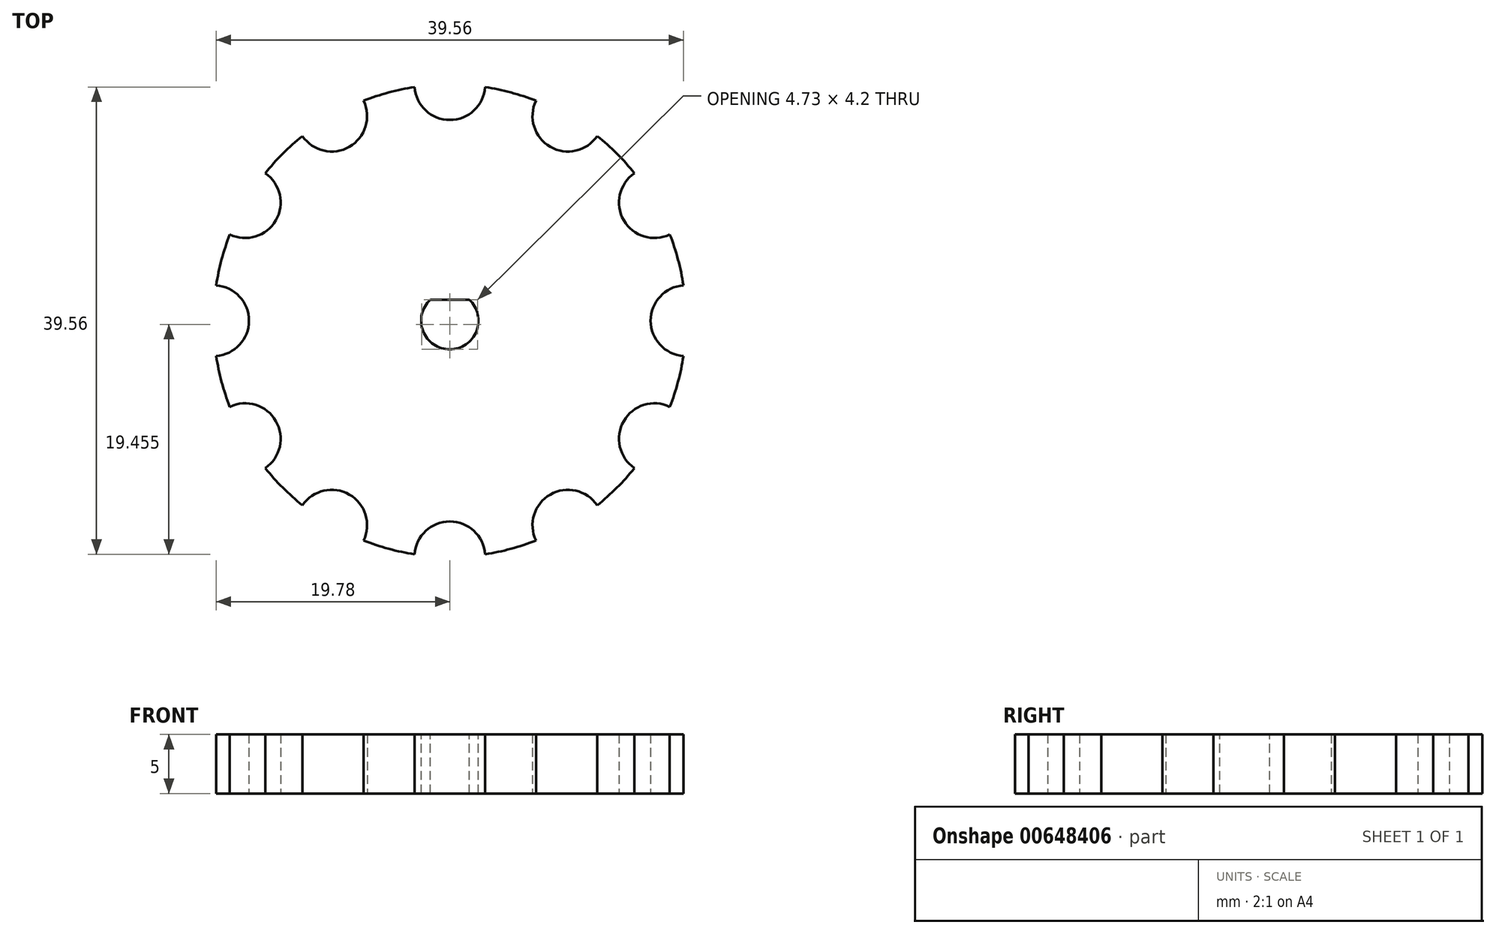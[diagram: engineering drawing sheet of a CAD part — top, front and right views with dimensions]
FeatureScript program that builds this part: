
annotation { "Feature Type Name" : "Feature", "Feature Type Description" : "" }
export const myFeature = defineFeature(function(context is Context, id is Id, definition is map)
    precondition{}
    {
        {
            var Q0;
            Q0=qCreatedBy(makeId("Top.planeOp"),FACE);
            var sketch = newSketch(context, id + "F0", { "sketchPlane" : qUnion([Q0])});
            skCircle(sketch, "E0", {"center": v(0, 0) * mm, "radius": 20 * mm});
            skCircle(sketch, "E1", {"center": v(0, 20) * mm, "radius": 3 * mm});
            skCircle(sketch, "E2.1.0", {"center": v(-10, 17.32) * mm, "radius": 3 * mm});
            skCircle(sketch, "E2.2.0", {"center": v(-17.32, 10) * mm, "radius": 3 * mm});
            skCircle(sketch, "E2.3.0", {"center": v(-20, 0) * mm, "radius": 3 * mm});
            skCircle(sketch, "E2.4.0", {"center": v(-17.32, -10) * mm, "radius": 3 * mm});
            skCircle(sketch, "E2.5.0", {"center": v(-10, -17.32) * mm, "radius": 3 * mm});
            skCircle(sketch, "E2.6.0", {"center": v(0, -20) * mm, "radius": 3 * mm});
            skCircle(sketch, "E2.7.0", {"center": v(10, -17.32) * mm, "radius": 3 * mm});
            skCircle(sketch, "E2.8.0", {"center": v(17.32, -10) * mm, "radius": 3 * mm});
            skCircle(sketch, "E2.9.0", {"center": v(20, 0) * mm, "radius": 3 * mm});
            skCircle(sketch, "E2.10.0", {"center": v(17.32, 10) * mm, "radius": 3 * mm});
            skCircle(sketch, "E2.11.0", {"center": v(10, 17.32) * mm, "radius": 3 * mm});
            skSolve(sketch);
        }
        {
            var Q0;
            {var subQ1=sQuery(id+"F0.wireOp",EDGE,"E0");var subQ33=sQuery(id+"F0.wireOp",EDGE,"E2.10.0");var subQ36=makeQuery(id+"F0.imprint","INTERSECT",VERTEX,{"disambiguationData":[OD(0.0)],"derivedFrom":[subQ1,subQ33]});Q0=makeQuery(id+"F0.imprint","IMPRINT",FACE,{"disambiguationData":[TD([[makeQuery(id+"F0.imprint","IMPRINT",EDGE,{"disambiguationData":[TD([[subQ36,1.0]])],"derivedFrom":subQ1}),1.0]])]});}
            extrude(context, id + "F1", {"entities" : qUnion([Q0]), "depth" : 5 * mm, "offsetDistance" : 25 * mm});
        }
        {
            var Q0;
            Q0=makeQuery(id+"F1.opExtrude","CAP_FACE",FACE,{"disambiguationData":[OSD([sQuery(id+"F0.wireOp",EDGE,"E0"),sQuery(id+"F0.wireOp",EDGE,"E1"),sQuery(id+"F0.wireOp",EDGE,"E2.1.0"),sQuery(id+"F0.wireOp",EDGE,"E2.2.0"),sQuery(id+"F0.wireOp",EDGE,"E2.3.0"),sQuery(id+"F0.wireOp",EDGE,"E2.4.0"),sQuery(id+"F0.wireOp",EDGE,"E2.5.0"),sQuery(id+"F0.wireOp",EDGE,"E2.6.0"),sQuery(id+"F0.wireOp",EDGE,"E2.7.0"),sQuery(id+"F0.wireOp",EDGE,"E2.8.0"),sQuery(id+"F0.wireOp",EDGE,"E2.9.0"),sQuery(id+"F0.wireOp",EDGE,"E2.10.0"),sQuery(id+"F0.wireOp",EDGE,"E2.11.0")])],"isStart":false});
            var sketch = newSketch(context, id + "F2", { "sketchPlane" : qUnion([Q0])});
            skArc(sketch, "E3", {"start": v(-1.65, 1.78) * mm, "mid": v(0, -2.43) * mm, "end": v(1.65, 1.78) * mm});
            skLineSegment(sketch, "E4", {"start": v(-1.65, 1.78) * mm, "end": v(1.65, 1.78) * mm});
            skSolve(sketch);
        }
        {
            var Q0;
            Q0=makeQuery(id+"F2.imprint","IMPRINT",FACE,{"disambiguationData":[TD([[makeQuery(id+"F2.imprint","IMPRINT",EDGE,{"derivedFrom":sQuery(id+"F2.wireOp",EDGE,"E3")}),1.0]])]});
            extrude(context, id + "F3", {"entities" : qUnion([Q0]), "operationType" : NewBodyOperationType.REMOVE, "endBound" : BoundingType.THROUGH_ALL, "oppositeDirection" : true, "depth" : 25 * mm, "offsetDistance" : 25 * mm});
        }
    });
